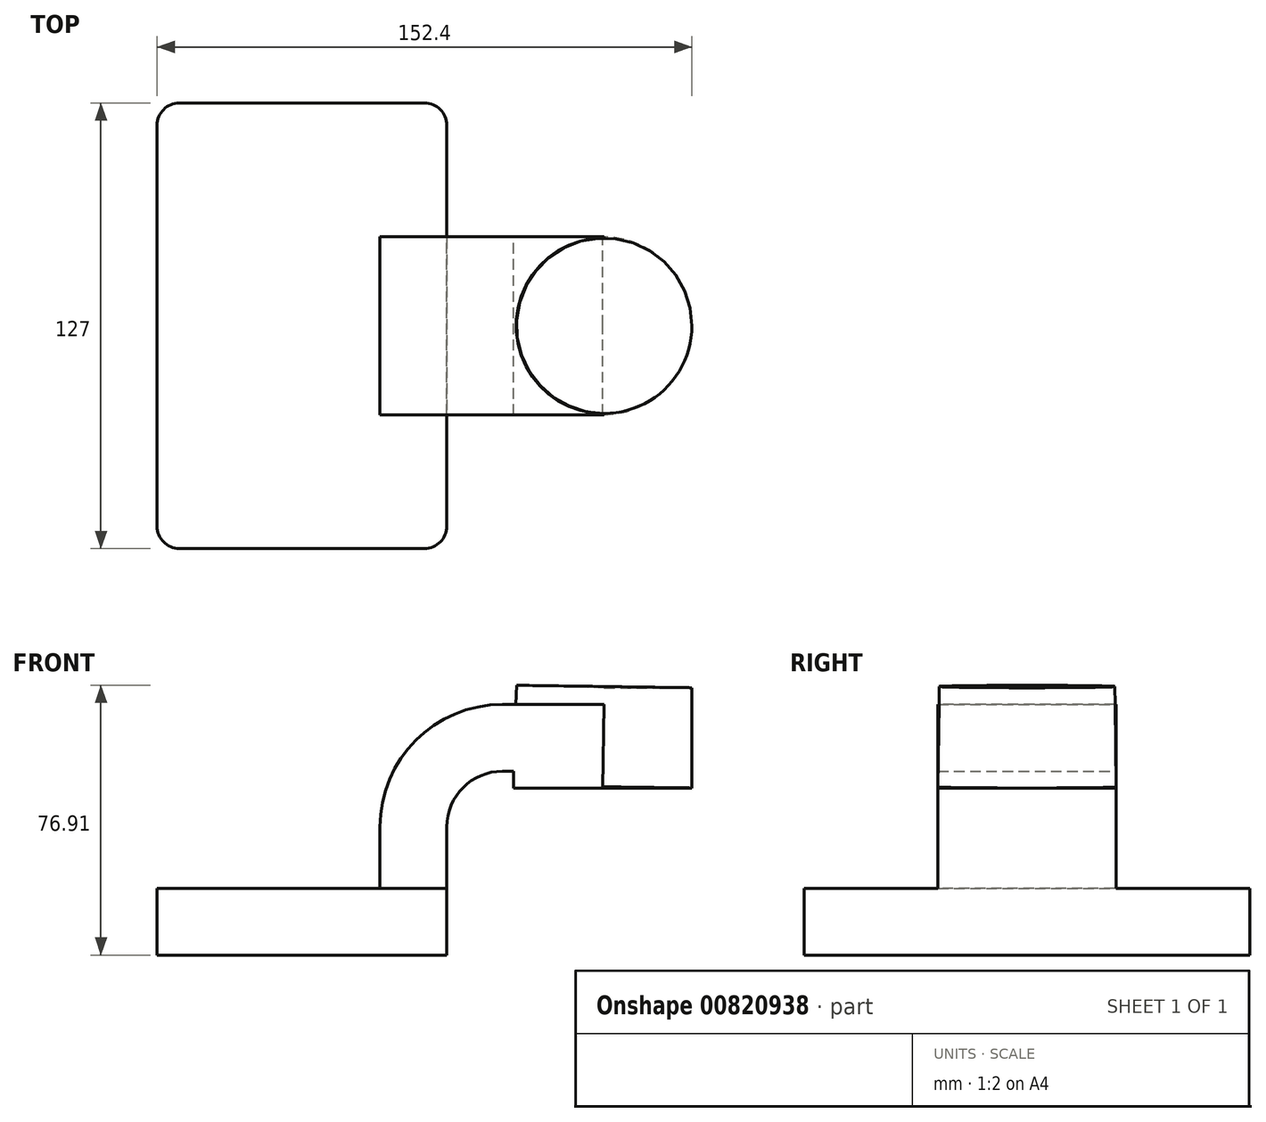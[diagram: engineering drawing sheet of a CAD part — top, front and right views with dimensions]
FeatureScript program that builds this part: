
annotation { "Feature Type Name" : "Feature", "Feature Type Description" : "" }
export const myFeature = defineFeature(function(context is Context, id is Id, definition is map)
    precondition{}
    {
        {
            var Q0;
            Q0=qCreatedBy(makeId("Front.planeOp"),FACE);
            var sketch = newSketch(context, id + "F0", { "sketchPlane" : qUnion([Q0])});
            skLineSegment(sketch, "E0.bottom", {"start": v(41.28, -9.52) * mm, "end": v(-41.27, -9.53) * mm});
            skLineSegment(sketch, "E0.top", {"start": v(41.27, 9.53) * mm, "end": v(-41.28, 9.53) * mm});
            skLineSegment(sketch, "E0.left", {"start": v(41.28, -9.52) * mm, "end": v(41.28, 9.53) * mm});
            skLineSegment(sketch, "E0.right", {"start": v(-41.27, -9.52) * mm, "end": v(-41.28, 9.53) * mm});
            skPoint(sketch, "E0.middle", {"position": v(0, 0) * mm});
            skLineSegment(sketch, "E1", {"start": v(41.27, 9.53) * mm, "end": v(41.27, 27) * mm});
            skArc(sketch, "E2", {"start": v(41.27, 27) * mm, "mid": v(45.92, 38.23) * mm, "end": v(57.15, 42.88) * mm});
            skLineSegment(sketch, "E3", {"start": v(57.15, 42.88) * mm, "end": v(85.49, 42.88) * mm});
            skLineSegment(sketch, "E4.bottom", {"start": v(111.12, 38.1) * mm, "end": v(60.32, 38.1) * mm});
            skLineSegment(sketch, "E4.top", {"start": v(111.12, 66.68) * mm, "end": v(60.32, 66.68) * mm});
            skLineSegment(sketch, "E4.left", {"start": v(111.12, 38.1) * mm, "end": v(111.12, 66.68) * mm});
            skLineSegment(sketch, "E4.right", {"start": v(60.32, 38.1) * mm, "end": v(60.32, 66.68) * mm});
            skPoint(sketch, "E4.middle", {"position": v(85.72, 52.39) * mm});
            skLineSegment(sketch, "E5.0", {"start": v(57.15, 61.93) * mm, "end": v(86.13, 61.93) * mm});
            skArc(sketch, "E5.1", {"start": v(22.23, 27) * mm, "mid": v(32.45, 51.7) * mm, "end": v(57.15, 61.93) * mm});
            skLineSegment(sketch, "E5.2", {"start": v(22.23, 9.53) * mm, "end": v(22.23, 27) * mm});
            skPoint(sketch, "E6.endSnap0", {"position": v(85.72, 38.1) * mm});
            skFitSpline(sketch, "E7", {"points": [v(-41.28, 9.53) * mm, v(57.15, 61.93) * mm], "startDerivative": vector(23.44, 154.43) * mm, "endDerivative": vector(117.91, -2.36) * mm});
            skLineSegment(sketch, "E8", {"start": v(86.13, 66.68) * mm, "end": v(85.72, 38.1) * mm});
            skSolve(sketch);
        }
        {
            var Q0;
            Q0=makeQuery(id+"F0.imprint","IMPRINT",FACE,{"disambiguationData":[TD([[makeQuery(id+"F0.imprint","IMPRINT",EDGE,{"derivedFrom":sQuery(id+"F0.wireOp",EDGE,"E0.bottom")}),-1.0]])]});
            extrude(context, id + "F1", {"entities" : qUnion([Q0]), "endBound" : BoundingType.SYMMETRIC, "oppositeDirection" : true, "depth" : 127 * mm, "offsetDistance" : 25.4 * mm});
        }
        {
            var Q0;
            {var subQ4=sQuery(id+"F0.wireOp",EDGE,"E1");Q0=makeQuery(id+"F0.imprint","IMPRINT",FACE,{"disambiguationData":[TD([[makeQuery(id+"F0.imprint","IMPRINT",EDGE,{"derivedFrom":subQ4}),1.0]])]});}
            var Q1;
            {var subQ1=sQuery(id+"F0.wireOp",EDGE,"E3");var subQ3=sQuery(id+"F0.wireOp",EDGE,"E4.right");var subQ4=makeQuery(id+"F0.imprint","INTERSECT",VERTEX,{"derivedFrom":[subQ1,subQ3]});Q1=makeQuery(id+"F0.imprint","IMPRINT",FACE,{"disambiguationData":[TD([[makeQuery(id+"F0.imprint","IMPRINT",EDGE,{"disambiguationData":[TD([[subQ4,-1.0]])],"derivedFrom":subQ3}),-1.0]])]});}
            extrude(context, id + "F2", {"entities" : qUnion([Q0, Q1]), "operationType" : NewBodyOperationType.ADD, "endBound" : BoundingType.SYMMETRIC, "depth" : 50.8 * mm, "offsetDistance" : 25.4 * mm});
        }
        {
            var Q0;
            Q0=makeQuery(id+"F0.imprint","IMPRINT",FACE,{"disambiguationData":[TD([[makeQuery(id+"F0.imprint","IMPRINT",EDGE,{"derivedFrom":sQuery(id+"F0.wireOp",EDGE,"E5.1")}),1.0]])]});
            extrude(context, id + "F3", {"entities" : qUnion([Q0]), "operationType" : NewBodyOperationType.ADD, "endBound" : BoundingType.SYMMETRIC, "depth" : 15.88 * mm, "offsetDistance" : 25.4 * mm});
        }
        {
            var Q0;
            {var subQ4=sQuery(id+"F0.wireOp",EDGE,"E4.left");Q0=makeQuery(id+"F0.imprint","IMPRINT",FACE,{"disambiguationData":[TD([[makeQuery(id+"F0.imprint","IMPRINT",EDGE,{"derivedFrom":subQ4}),1.0]])]});}
            var Q1;
            Q1=sQuery(id+"F0.wireOp",EDGE,"E8");
            revolve(context, id + "F4", {"operationType" : NewBodyOperationType.ADD, "surfaceOperationType" : NewSurfaceOperationType.NEW, "entities" : qUnion([Q0]), "axis" : qUnion([Q1]), "revolveType" : RevolveType.FULL});
        }
        {
            var Q0;
            Q0=makeQuery(id+"F1.opExtrude","CAP_EDGE",EDGE,{"disambiguationData":[OSD([sQuery(id+"F0.wireOp",EDGE,"E0.right")])],"isStart":true});
            var Q1;
            Q1=makeQuery(id+"F1.opExtrude","CAP_EDGE",EDGE,{"disambiguationData":[OSD([sQuery(id+"F0.wireOp",EDGE,"E0.left")])],"isStart":true});
            var Q2;
            Q2=makeQuery(id+"F1.opExtrude","CAP_EDGE",EDGE,{"disambiguationData":[OSD([sQuery(id+"F0.wireOp",EDGE,"E0.left")])],"isStart":false});
            var Q3;
            Q3=makeQuery(id+"F1.opExtrude","CAP_EDGE",EDGE,{"disambiguationData":[OSD([sQuery(id+"F0.wireOp",EDGE,"E0.right")])],"isStart":false});
            fillet(context, id + "F5", {"entities" : qUnion([Q0, Q1, Q2, Q3]), "radius" : 6.35 * mm, "tangentPropagation" : true, "allowEdgeOverflow" : false});
        }
    });
